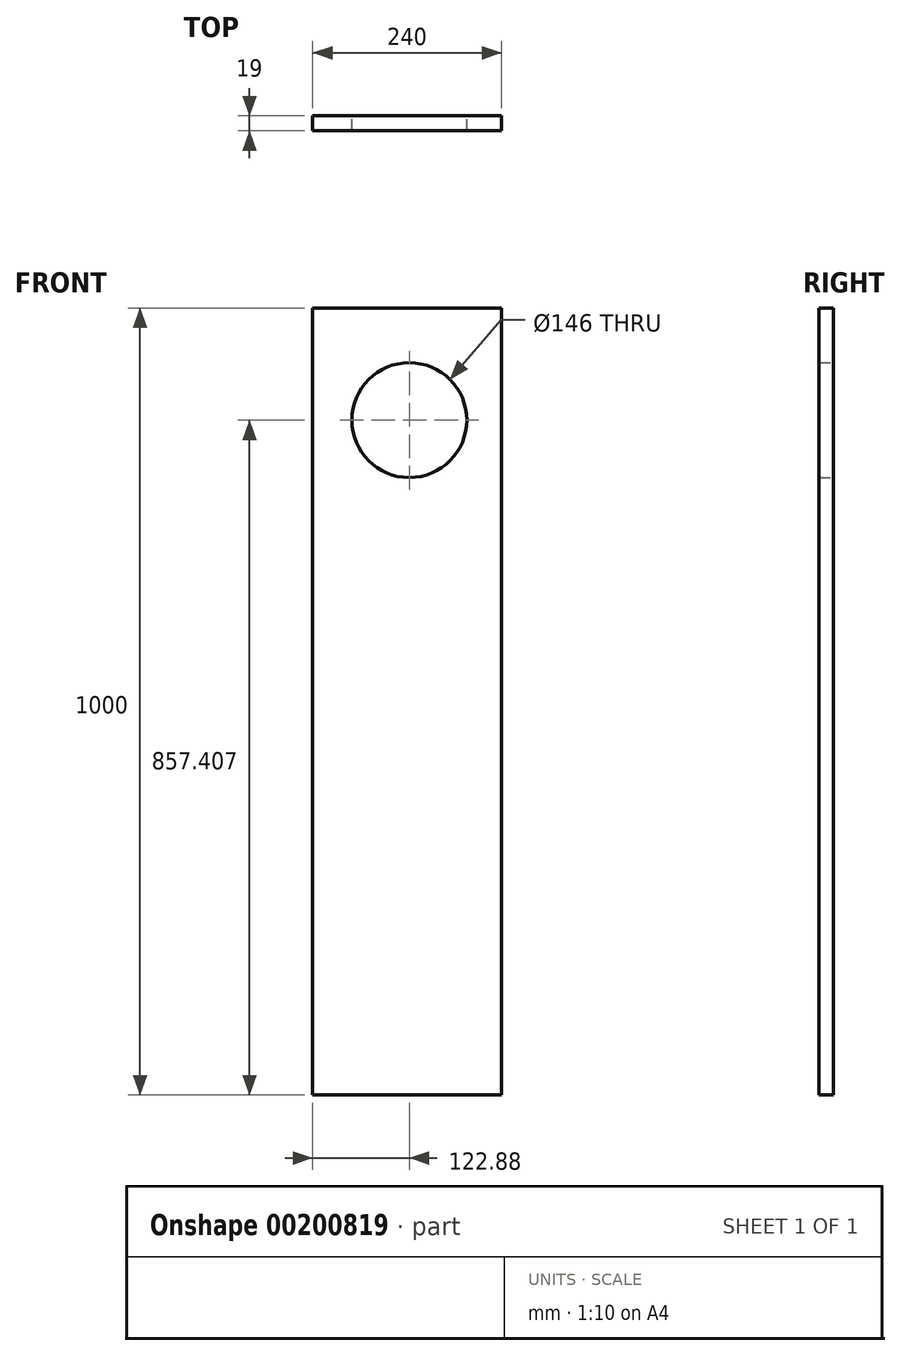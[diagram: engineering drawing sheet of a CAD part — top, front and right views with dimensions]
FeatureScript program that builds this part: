
annotation { "Feature Type Name" : "Feature", "Feature Type Description" : "" }
export const myFeature = defineFeature(function(context is Context, id is Id, definition is map)
    precondition{}
    {
        {
            var Q0;
            Q0=qCreatedBy(makeId("Front.planeOp"),FACE);
            var sketch = newSketch(context, id + "F0", { "sketchPlane" : qUnion([Q0])});
            skLineSegment(sketch, "E0.bottom", {"start": v(-122.88, 809.45) * mm, "end": v(117.12, 809.45) * mm});
            skLineSegment(sketch, "E0.top", {"start": v(-122.88, -190.55) * mm, "end": v(117.12, -190.55) * mm});
            skLineSegment(sketch, "E0.left", {"start": v(-122.88, 809.45) * mm, "end": v(-122.88, -190.55) * mm});
            skLineSegment(sketch, "E0.right", {"start": v(117.12, 809.45) * mm, "end": v(117.12, -190.55) * mm});
            skPoint(sketch, "E1", {"position": v(0, 809.45) * mm});
            skPoint(sketch, "E2", {"position": v(-2.88, -190.55) * mm});
            skCircle(sketch, "E3", {"center": v(0, 666.86) * mm, "radius": 73 * mm});
            skSolve(sketch);
        }
        {
            var Q0;
            Q0=makeQuery(id+"F0.imprint","IMPRINT",FACE,{"disambiguationData":[TD([[makeQuery(id+"F0.imprint","IMPRINT",EDGE,{"derivedFrom":sQuery(id+"F0.wireOp",EDGE,"E0.bottom")}),-1.0]])]});
            extrude(context, id + "F1", {"entities" : qUnion([Q0]), "depth" : 19 * mm});
        }
    });
